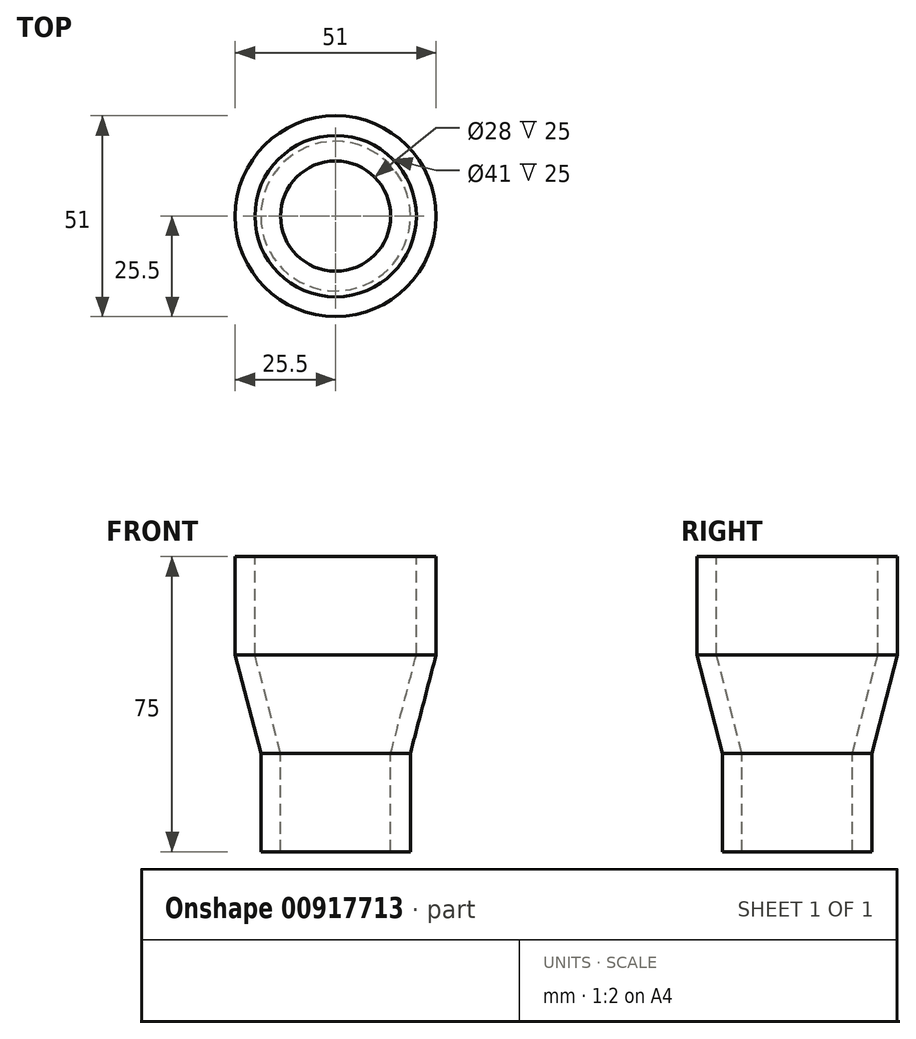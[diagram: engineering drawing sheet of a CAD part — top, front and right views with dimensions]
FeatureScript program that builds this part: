
annotation { "Feature Type Name" : "Feature", "Feature Type Description" : "" }
export const myFeature = defineFeature(function(context is Context, id is Id, definition is map)
    precondition{}
    {
        {
            var Q0;
            Q0=qCreatedBy(makeId("Front.planeOp"),FACE);
            var sketch = newSketch(context, id + "F0", { "sketchPlane" : qUnion([Q0])});
            skLineSegment(sketch, "E0", {"start": v(0, 63.06) * mm, "end": v(0, -56.94) * mm, "construction": true});
            skPoint(sketch, "E1", {"position": v(-14, -25) * mm});
            skPoint(sketch, "E2", {"position": v(-19, -25) * mm});
            skPoint(sketch, "E3", {"position": v(-19, 0) * mm});
            skPoint(sketch, "E4", {"position": v(-14, 0) * mm});
            skPoint(sketch, "E5", {"position": v(-25.5, 25) * mm});
            skPoint(sketch, "E6", {"position": v(-20.5, 25) * mm});
            skPoint(sketch, "E7", {"position": v(-25.5, 50) * mm});
            skPoint(sketch, "E8", {"position": v(-20.5, 50) * mm});
            skPoint(sketch, "E9", {"position": v(0, 0) * mm});
            skLineSegment(sketch, "E10", {"start": v(-25.5, 50) * mm, "end": v(-25.5, 25) * mm});
            skLineSegment(sketch, "E11", {"start": v(-25.5, 25) * mm, "end": v(-19, 0) * mm});
            skLineSegment(sketch, "E12", {"start": v(-19, 0) * mm, "end": v(-19, -25) * mm});
            skLineSegment(sketch, "E13", {"start": v(-19, -25) * mm, "end": v(-14, -25) * mm});
            skLineSegment(sketch, "E14", {"start": v(-14, -25) * mm, "end": v(-14, 0) * mm});
            skLineSegment(sketch, "E15", {"start": v(-14, 0) * mm, "end": v(-20.5, 25) * mm});
            skLineSegment(sketch, "E16", {"start": v(-20.5, 25) * mm, "end": v(-20.5, 50) * mm});
            skLineSegment(sketch, "E17", {"start": v(-20.5, 50) * mm, "end": v(-25.5, 50) * mm});
            skSolve(sketch);
        }
        {
            var Q0;
            Q0=makeQuery(id+"F0.imprint","IMPRINT",FACE,{"disambiguationData":[TD([[makeQuery(id+"F0.imprint","IMPRINT",EDGE,{"derivedFrom":sQuery(id+"F0.wireOp",EDGE,"E10")}),1.0]])]});
            var Q1;
            Q1=sQuery(id+"F0.wireOp",EDGE,"E0");
            revolve(context, id + "F1", {"surfaceOperationType" : NewSurfaceOperationType.NEW, "entities" : qUnion([Q0]), "axis" : qUnion([Q1]), "revolveType" : RevolveType.FULL});
        }
    });
